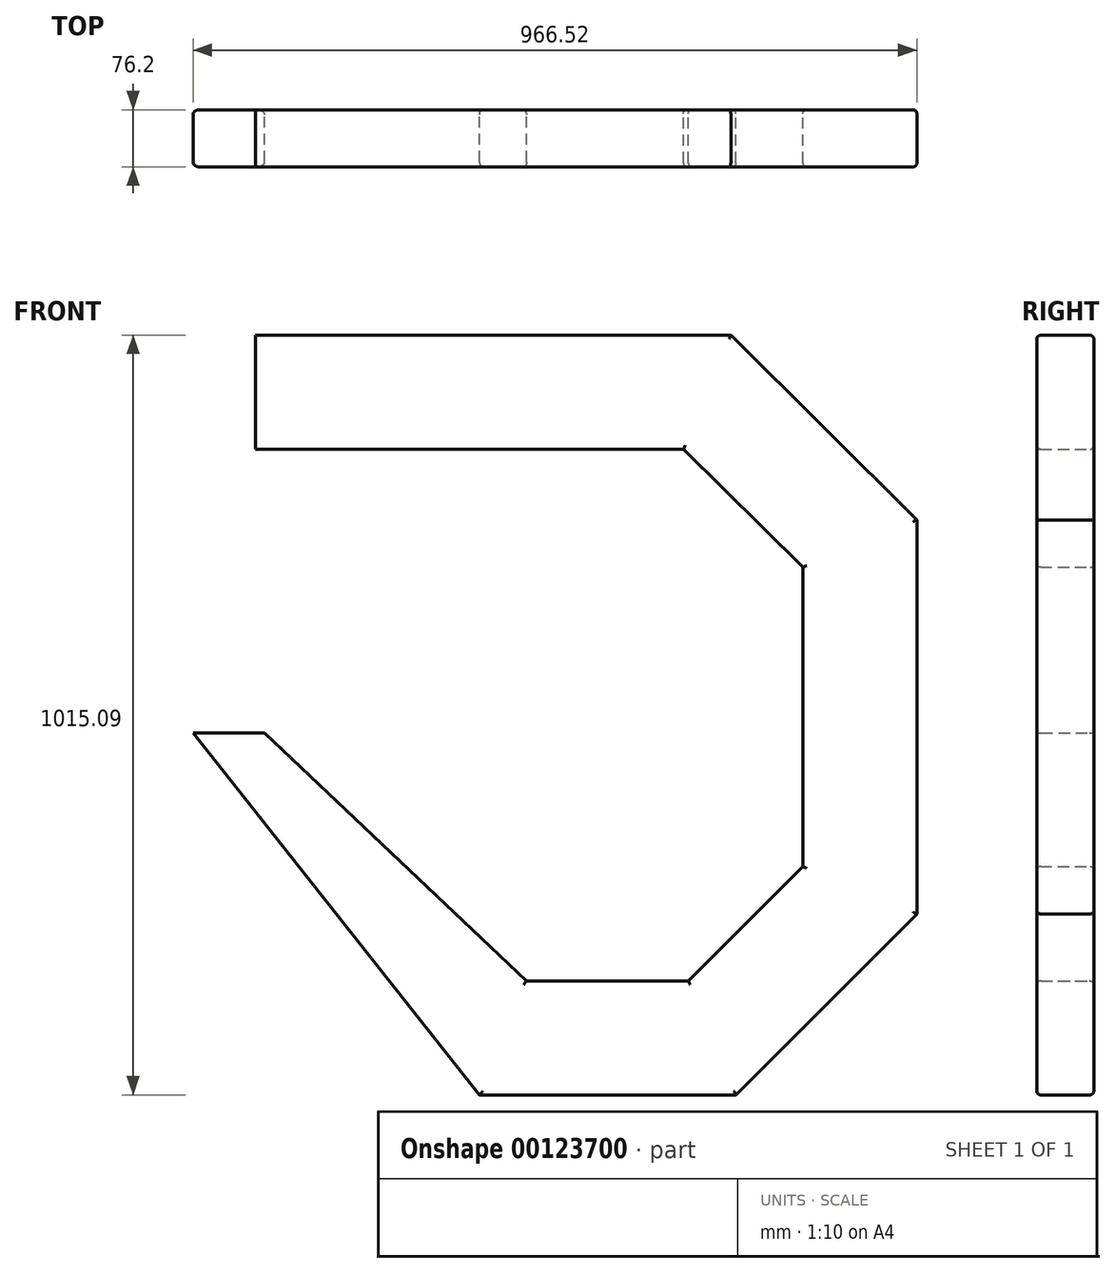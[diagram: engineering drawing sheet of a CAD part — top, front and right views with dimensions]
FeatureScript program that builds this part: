
annotation { "Feature Type Name" : "Feature", "Feature Type Description" : "" }
export const myFeature = defineFeature(function(context is Context, id is Id, definition is map)
    precondition{}
    {
        {
            var Q0;
            Q0=qCreatedBy(makeId("Front.planeOp"),FACE);
            var sketch = newSketch(context, id + "F0", { "sketchPlane" : qUnion([Q0])});
            skLineSegment(sketch, "E0", {"start": v(-527.2, 291.35) * mm, "end": v(107.43, 291.35) * mm});
            skLineSegment(sketch, "E1", {"start": v(107.43, 291.35) * mm, "end": v(44.3, 138.95) * mm});
            skLineSegment(sketch, "E2", {"start": v(44.3, 138.95) * mm, "end": v(-527.2, 138.95) * mm});
            skLineSegment(sketch, "E3", {"start": v(-527.2, 138.95) * mm, "end": v(-527.2, 291.35) * mm});
            skLineSegment(sketch, "E4", {"start": v(44.3, 138.95) * mm, "end": v(203.48, -18.63) * mm});
            skLineSegment(sketch, "E5", {"start": v(203.48, -18.63) * mm, "end": v(355.88, 44.5) * mm});
            skLineSegment(sketch, "E6", {"start": v(355.88, 44.5) * mm, "end": v(107.43, 291.35) * mm});
            skLineSegment(sketch, "E7", {"start": v(203.48, -18.63) * mm, "end": v(203.48, -418.68) * mm});
            skLineSegment(sketch, "E8", {"start": v(203.48, -418.68) * mm, "end": v(355.88, -481.8) * mm});
            skLineSegment(sketch, "E9", {"start": v(355.88, -481.8) * mm, "end": v(355.88, 44.5) * mm});
            skLineSegment(sketch, "E10", {"start": v(203.48, -418.68) * mm, "end": v(50.81, -571.34) * mm});
            skLineSegment(sketch, "E11", {"start": v(50.81, -571.34) * mm, "end": v(113.94, -723.74) * mm});
            skLineSegment(sketch, "E12", {"start": v(113.94, -723.74) * mm, "end": v(355.88, -481.8) * mm});
            skLineSegment(sketch, "E13", {"start": v(50.81, -571.34) * mm, "end": v(-165.09, -571.34) * mm});
            skLineSegment(sketch, "E14", {"start": v(-165.09, -571.34) * mm, "end": v(-228.21, -723.74) * mm});
            skLineSegment(sketch, "E15", {"start": v(-228.21, -723.74) * mm, "end": v(113.94, -723.74) * mm});
            skLineSegment(sketch, "E16", {"start": v(203.48, -239.97) * mm, "end": v(-515.4, -239.97) * mm, "construction": true});
            skLineSegment(sketch, "E17", {"start": v(-515.4, -239.97) * mm, "end": v(-515.4, 138.95) * mm, "construction": true});
            skLineSegment(sketch, "E18", {"start": v(-165.09, -571.34) * mm, "end": v(-515.4, -239.97) * mm});
            skLineSegment(sketch, "E19", {"start": v(-515.4, -239.97) * mm, "end": v(-610.64, -239.97) * mm});
            skLineSegment(sketch, "E20", {"start": v(-610.64, -239.97) * mm, "end": v(-228.21, -723.74) * mm});
            skSolve(sketch);
        }
        {
            var Q0;
            Q0=makeQuery(id+"F0.imprint","IMPRINT",FACE,{"disambiguationData":[TD([[makeQuery(id+"F0.imprint","IMPRINT",EDGE,{"derivedFrom":sQuery(id+"F0.wireOp",EDGE,"E0")}),-1.0]])]});
            var Q1;
            Q1=makeQuery(id+"F0.imprint","IMPRINT",FACE,{"disambiguationData":[TD([[makeQuery(id+"F0.imprint","IMPRINT",EDGE,{"derivedFrom":sQuery(id+"F0.wireOp",EDGE,"E1")}),1.0]])]});
            var Q2;
            Q2=makeQuery(id+"F0.imprint","IMPRINT",FACE,{"disambiguationData":[TD([[makeQuery(id+"F0.imprint","IMPRINT",EDGE,{"derivedFrom":sQuery(id+"F0.wireOp",EDGE,"E5")}),-1.0]])]});
            var Q3;
            Q3=makeQuery(id+"F0.imprint","IMPRINT",FACE,{"disambiguationData":[TD([[makeQuery(id+"F0.imprint","IMPRINT",EDGE,{"derivedFrom":sQuery(id+"F0.wireOp",EDGE,"E8")}),-1.0]])]});
            var Q4;
            Q4=makeQuery(id+"F0.imprint","IMPRINT",FACE,{"disambiguationData":[TD([[makeQuery(id+"F0.imprint","IMPRINT",EDGE,{"derivedFrom":sQuery(id+"F0.wireOp",EDGE,"E11")}),-1.0]])]});
            extrude(context, id + "F1", {"entities" : qUnion([Q0, Q1, Q2, Q3, Q4]), "depth" : 76.2 * mm});
        }
        {
            var Q0;
            Q0=makeQuery(id+"F1.opExtrude","CAP_EDGE",EDGE,{"disambiguationData":[OSD([sQuery(id+"F0.wireOp",EDGE,"E0")])],"isStart":true});
            var Q1;
            Q1=makeQuery(id+"F1.opExtrude","CAP_EDGE",EDGE,{"disambiguationData":[OSD([sQuery(id+"F0.wireOp",EDGE,"E6")])],"isStart":true});
            var Q2;
            Q2=makeQuery(id+"F1.opExtrude","CAP_EDGE",EDGE,{"disambiguationData":[OSD([sQuery(id+"F0.wireOp",EDGE,"E9")])],"isStart":true});
            var Q3;
            Q3=makeQuery(id+"F1.opExtrude","CAP_EDGE",EDGE,{"disambiguationData":[OSD([sQuery(id+"F0.wireOp",EDGE,"E12")])],"isStart":true});
            var Q4;
            Q4=makeQuery(id+"F1.opExtrude","CAP_EDGE",EDGE,{"disambiguationData":[OSD([sQuery(id+"F0.wireOp",EDGE,"E15")])],"isStart":true});
            var Q5;
            Q5=makeQuery(id+"F1.opExtrude","CAP_EDGE",EDGE,{"disambiguationData":[OSD([sQuery(id+"F0.wireOp",EDGE,"E13")])],"isStart":true});
            var Q6;
            Q6=makeQuery(id+"F1.opExtrude","CAP_EDGE",EDGE,{"disambiguationData":[OSD([sQuery(id+"F0.wireOp",EDGE,"E10")])],"isStart":true});
            var Q7;
            Q7=makeQuery(id+"F1.opExtrude","CAP_EDGE",EDGE,{"disambiguationData":[OSD([sQuery(id+"F0.wireOp",EDGE,"E7")])],"isStart":true});
            var Q8;
            Q8=makeQuery(id+"F1.opExtrude","CAP_EDGE",EDGE,{"disambiguationData":[OSD([sQuery(id+"F0.wireOp",EDGE,"E4")])],"isStart":true});
            var Q9;
            Q9=makeQuery(id+"F1.opExtrude","CAP_EDGE",EDGE,{"disambiguationData":[OSD([sQuery(id+"F0.wireOp",EDGE,"E2")])],"isStart":true});
            var Q10;
            Q10=makeQuery(id+"F1.opExtrude","CAP_EDGE",EDGE,{"disambiguationData":[OSD([sQuery(id+"F0.wireOp",EDGE,"E0")])],"isStart":false});
            var Q11;
            Q11=makeQuery(id+"F1.opExtrude","CAP_EDGE",EDGE,{"disambiguationData":[OSD([sQuery(id+"F0.wireOp",EDGE,"E6")])],"isStart":false});
            var Q12;
            Q12=makeQuery(id+"F1.opExtrude","CAP_EDGE",EDGE,{"disambiguationData":[OSD([sQuery(id+"F0.wireOp",EDGE,"E2")])],"isStart":false});
            var Q13;
            Q13=makeQuery(id+"F1.opExtrude","CAP_EDGE",EDGE,{"disambiguationData":[OSD([sQuery(id+"F0.wireOp",EDGE,"E4")])],"isStart":false});
            var Q14;
            Q14=makeQuery(id+"F1.opExtrude","CAP_EDGE",EDGE,{"disambiguationData":[OSD([sQuery(id+"F0.wireOp",EDGE,"E7")])],"isStart":false});
            var Q15;
            Q15=makeQuery(id+"F1.opExtrude","CAP_EDGE",EDGE,{"disambiguationData":[OSD([sQuery(id+"F0.wireOp",EDGE,"E10")])],"isStart":false});
            var Q16;
            Q16=makeQuery(id+"F1.opExtrude","CAP_EDGE",EDGE,{"disambiguationData":[OSD([sQuery(id+"F0.wireOp",EDGE,"E13")])],"isStart":false});
            var Q17;
            Q17=makeQuery(id+"F1.opExtrude","CAP_EDGE",EDGE,{"disambiguationData":[OSD([sQuery(id+"F0.wireOp",EDGE,"E9")])],"isStart":false});
            var Q18;
            Q18=makeQuery(id+"F1.opExtrude","CAP_EDGE",EDGE,{"disambiguationData":[OSD([sQuery(id+"F0.wireOp",EDGE,"E12")])],"isStart":false});
            var Q19;
            Q19=makeQuery(id+"F1.opExtrude","CAP_EDGE",EDGE,{"disambiguationData":[OSD([sQuery(id+"F0.wireOp",EDGE,"E15")])],"isStart":false});
            fillet(context, id + "F2", {"entities" : qUnion([Q0, Q1, Q2, Q3, Q4, Q5, Q6, Q7, Q8, Q9, Q10, Q11, Q12, Q13, Q14, Q15, Q16, Q17, Q18, Q19]), "radius" : 5.08 * mm, "tangentPropagation" : true, "allowEdgeOverflow" : false});
        }
        {
            var Q0;
            Q0=makeQuery(id+"F0.imprint","IMPRINT",FACE,{"disambiguationData":[TD([[makeQuery(id+"F0.imprint","IMPRINT",EDGE,{"derivedFrom":sQuery(id+"F0.wireOp",EDGE,"E14")}),-1.0]])]});
            extrude(context, id + "F3", {"entities" : qUnion([Q0]), "operationType" : NewBodyOperationType.ADD, "depth" : 76.2 * mm});
        }
        {
            var Q0;
            Q0=makeQuery(id+"F3.opExtrude","CAP_EDGE",EDGE,{"disambiguationData":[OSD([sQuery(id+"F0.wireOp",EDGE,"E20")])],"isStart":false});
            var Q1;
            Q1=makeQuery(id+"F3.opExtrude","CAP_EDGE",EDGE,{"disambiguationData":[OSD([sQuery(id+"F0.wireOp",EDGE,"E18")])],"isStart":false});
            var Q2;
            Q2=makeQuery(id+"F3.opExtrude","CAP_EDGE",EDGE,{"disambiguationData":[OSD([sQuery(id+"F0.wireOp",EDGE,"E18")])],"isStart":true});
            var Q3;
            Q3=makeQuery(id+"F3.opExtrude","CAP_EDGE",EDGE,{"disambiguationData":[OSD([sQuery(id+"F0.wireOp",EDGE,"E20")])],"isStart":true});
            fillet(context, id + "F4", {"entities" : qUnion([Q0, Q1, Q2, Q3]), "radius" : 6.35 * mm, "tangentPropagation" : true, "allowEdgeOverflow" : false});
        }
    });
